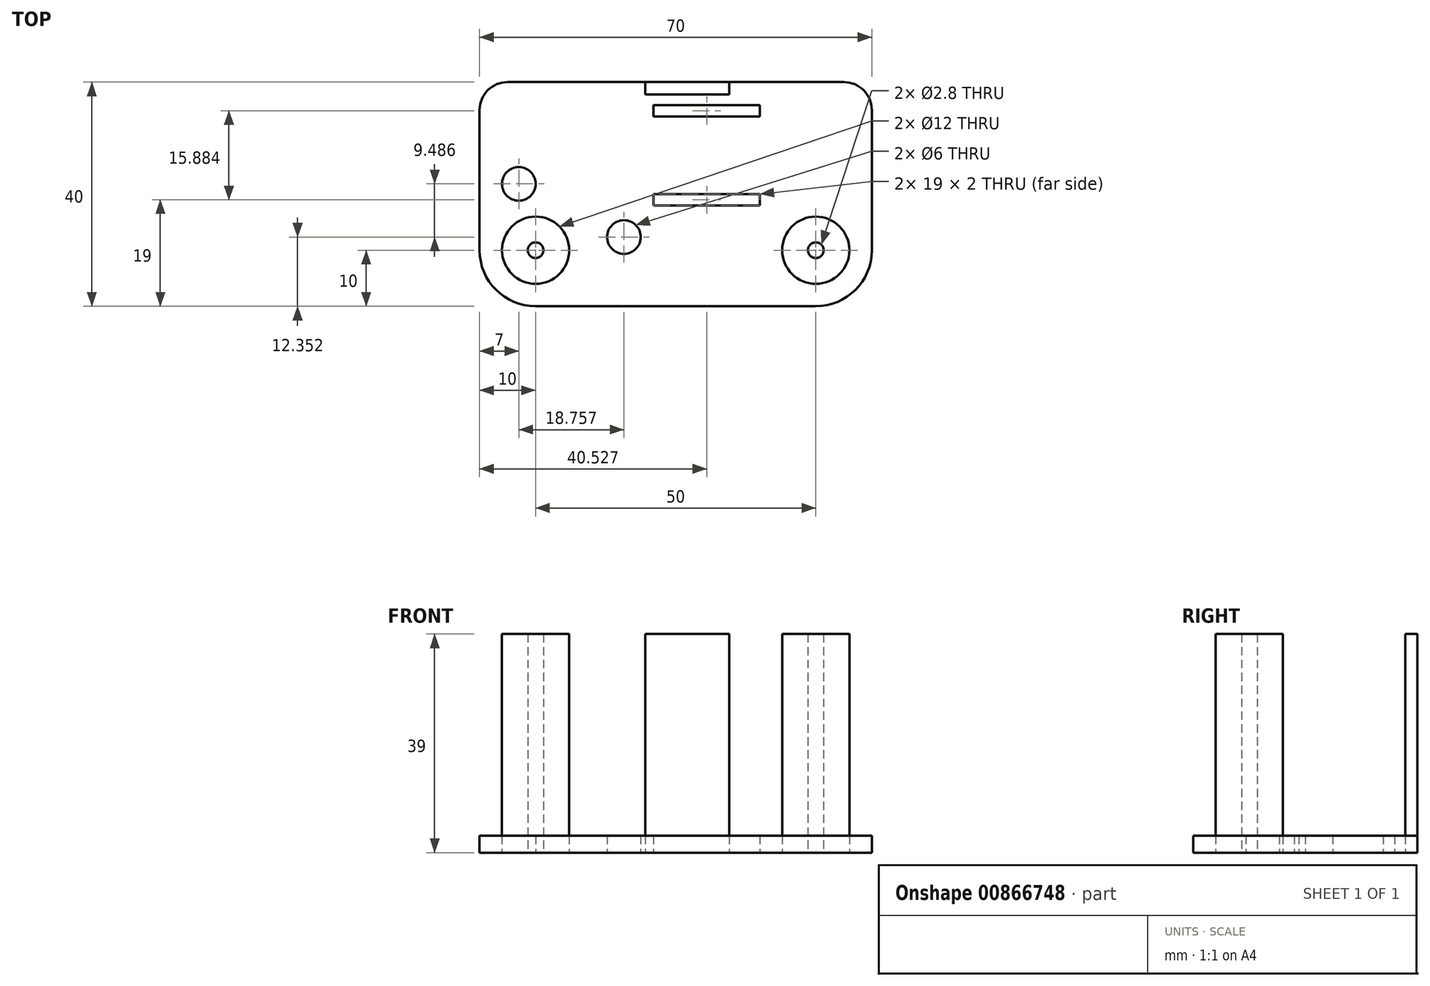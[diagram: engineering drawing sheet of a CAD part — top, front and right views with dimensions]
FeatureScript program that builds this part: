
annotation { "Feature Type Name" : "Feature", "Feature Type Description" : "" }
export const myFeature = defineFeature(function(context is Context, id is Id, definition is map)
    precondition{}
    {
        {
            var Q0;
            Q0=qCreatedBy(makeId("Top.planeOp"),FACE);
            var sketch = newSketch(context, id + "F0", { "sketchPlane" : qUnion([Q0])});
            skLineSegment(sketch, "E0.bottom", {"start": v(30, 20) * mm, "end": v(-30, 20) * mm});
            skLineSegment(sketch, "E0.top", {"start": v(25, -20) * mm, "end": v(-25, -20) * mm});
            skLineSegment(sketch, "E0.left", {"start": v(35, 15) * mm, "end": v(35, -10) * mm});
            skLineSegment(sketch, "E0.right", {"start": v(-35, 15) * mm, "end": v(-35, -10) * mm});
            skPoint(sketch, "E0.middle", {"position": v(0, 0) * mm});
            skLineSegment(sketch, "E1.top", {"start": v(35, -10) * mm, "end": v(25, -10) * mm, "construction": true});
            skLineSegment(sketch, "E1.right", {"start": v(25, -20) * mm, "end": v(25, -10) * mm, "construction": true});
            skCircle(sketch, "E2", {"center": v(25, -10) * mm, "radius": 6 * mm});
            skCircle(sketch, "E3", {"center": v(25, -10) * mm, "radius": 1.4 * mm});
            skLineSegment(sketch, "E4.top", {"start": v(-35, -10) * mm, "end": v(-25, -10) * mm, "construction": true});
            skLineSegment(sketch, "E4.right", {"start": v(-25, -20) * mm, "end": v(-25, -10) * mm, "construction": true});
            skCircle(sketch, "E5", {"center": v(-25, -10) * mm, "radius": 6 * mm});
            skCircle(sketch, "E6", {"center": v(-25, -10) * mm, "radius": 1.4 * mm});
            skLineSegment(sketch, "E7.bottom", {"start": v(-5.43, 20) * mm, "end": v(9.57, 20) * mm});
            skLineSegment(sketch, "E7.top", {"start": v(-5.43, 17.8) * mm, "end": v(9.57, 17.8) * mm});
            skLineSegment(sketch, "E7.left", {"start": v(-5.43, 20) * mm, "end": v(-5.43, 17.8) * mm});
            skLineSegment(sketch, "E7.right", {"start": v(9.57, 20) * mm, "end": v(9.57, 17.8) * mm});
            skPoint(sketch, "E8.visualSharp", {"position": v(-35, 20) * mm});
            skArc(sketch, "E8.filletArc", {"start": v(-30, 20) * mm, "mid": v(-33.54, 18.54) * mm, "end": v(-35, 15) * mm});
            skPoint(sketch, "E9.visualSharp", {"position": v(35, 20) * mm});
            skArc(sketch, "E9.filletArc", {"start": v(35, 15) * mm, "mid": v(33.54, 18.54) * mm, "end": v(30, 20) * mm});
            skPoint(sketch, "E10.visualSharp", {"position": v(35, -20) * mm});
            skArc(sketch, "E10.filletArc", {"start": v(25, -20) * mm, "mid": v(32.07, -17.07) * mm, "end": v(35, -10) * mm});
            skPoint(sketch, "E11.visualSharp", {"position": v(-35, -20) * mm});
            skArc(sketch, "E11.filletArc", {"start": v(-35, -10) * mm, "mid": v(-32.07, -17.07) * mm, "end": v(-25, -20) * mm});
            skCircle(sketch, "E12", {"center": v(-9.24, -7.65) * mm, "radius": 3 * mm});
            skCircle(sketch, "E13", {"center": v(-28, 1.84) * mm, "radius": 3 * mm});
            skLineSegment(sketch, "E14.bottom", {"start": v(15.03, 0) * mm, "end": v(-3.97, 0) * mm});
            skLineSegment(sketch, "E14.top", {"start": v(15.03, -2) * mm, "end": v(-3.97, -2) * mm});
            skLineSegment(sketch, "E14.left", {"start": v(15.03, 0) * mm, "end": v(15.03, -2) * mm});
            skLineSegment(sketch, "E14.right", {"start": v(-3.97, 0) * mm, "end": v(-3.97, -2) * mm});
            skLineSegment(sketch, "E15.bottom", {"start": v(-3.97, 15.88) * mm, "end": v(15.03, 15.88) * mm});
            skLineSegment(sketch, "E15.top", {"start": v(-3.97, 13.88) * mm, "end": v(15.03, 13.88) * mm});
            skLineSegment(sketch, "E15.left", {"start": v(-3.97, 15.88) * mm, "end": v(-3.97, 13.88) * mm});
            skLineSegment(sketch, "E15.right", {"start": v(15.03, 15.88) * mm, "end": v(15.03, 13.88) * mm});
            skSolve(sketch);
        }
        {
            var Q0;
            Q0=makeQuery(id+"F0.imprint","IMPRINT",FACE,{"disambiguationData":[TD([[makeQuery(id+"F0.imprint","IMPRINT",EDGE,{"derivedFrom":sQuery(id+"F0.wireOp",EDGE,"E2")}),1.0]])]});
            var Q1;
            Q1=makeQuery(id+"F0.imprint","IMPRINT",FACE,{"disambiguationData":[TD([[makeQuery(id+"F0.imprint","IMPRINT",EDGE,{"derivedFrom":sQuery(id+"F0.wireOp",EDGE,"E5")}),1.0]])]});
            var Q2;
            Q2=makeQuery(id+"F0.imprint","IMPRINT",FACE,{"disambiguationData":[TD([[makeQuery(id+"F0.imprint","IMPRINT",EDGE,{"derivedFrom":sQuery(id+"F0.wireOp",EDGE,"E7.top")}),1.0]])]});
            extrude(context, id + "F1", {"entities" : qUnion([Q0, Q1, Q2]), "depth" : 39 * mm, "offsetDistance" : 25 * mm});
        }
        {
            var Q0;
            {var subQ6=makeQuery(id+"F0.imprint","IMPRINT",EDGE,{"derivedFrom":sQuery(id+"F0.wireOp",EDGE,"E7.top")});Q0=qUnion([makeQuery(id+"F0.imprint","IMPRINT",FACE,{"disambiguationData":[TD([[makeQuery(id+"F0.imprint","IMPRINT",EDGE,{"derivedFrom":sQuery(id+"F0.wireOp",EDGE,"E0.top")}),-1.0]])]}),makeQuery(id+"F0.imprint","IMPRINT",FACE,{"disambiguationData":[TD([[subQ6,1.0]])]})]);}
            extrude(context, id + "F2", {"entities" : qUnion([Q0]), "depth" : 3 * mm, "offsetDistance" : 25 * mm});
        }
    });
